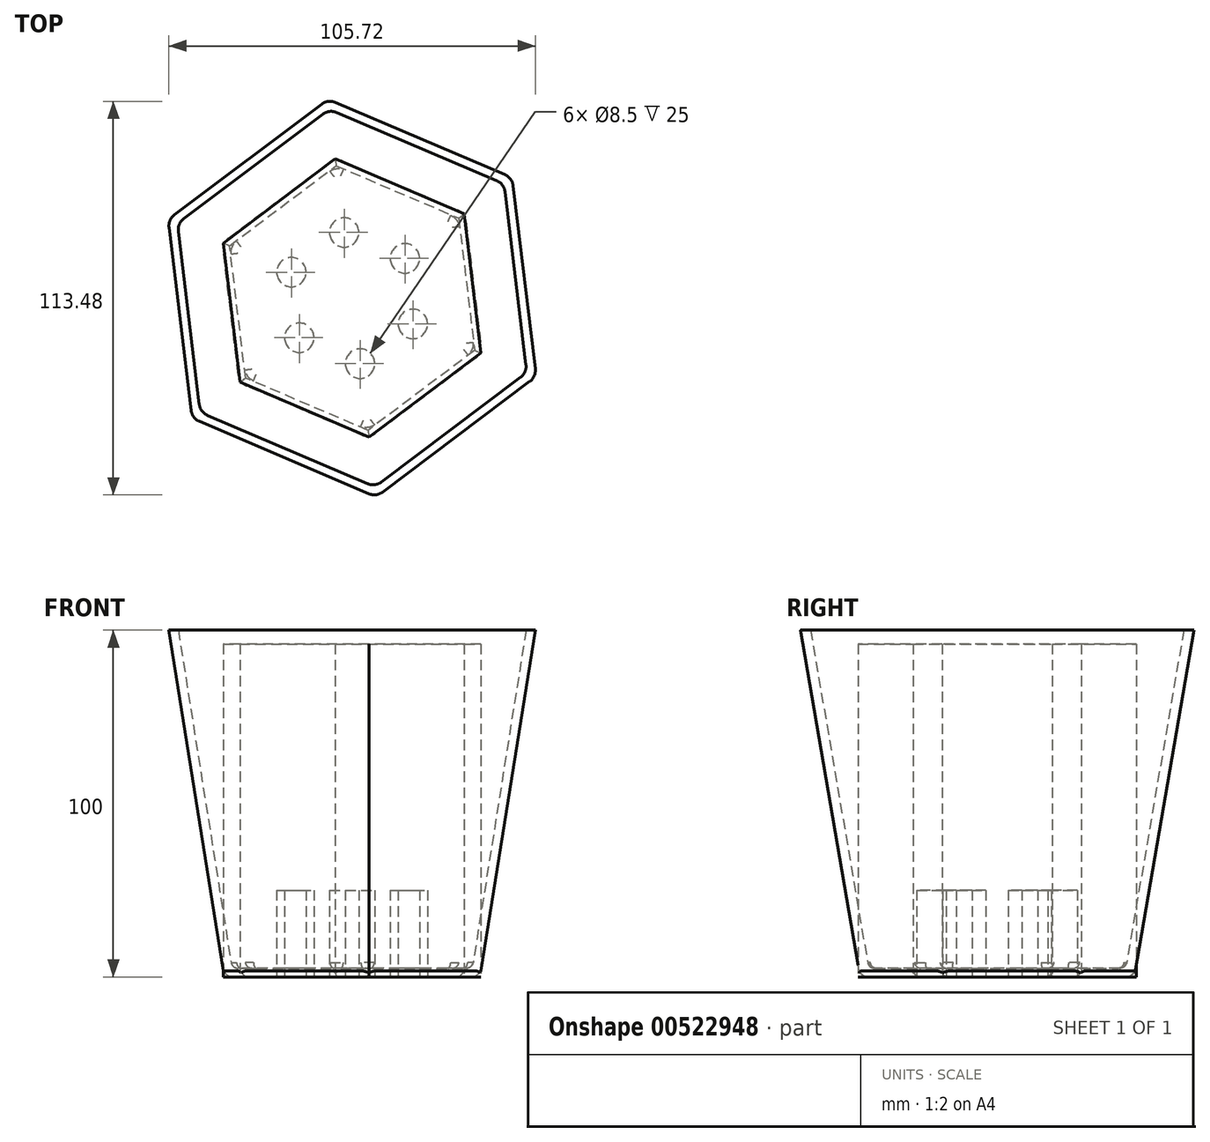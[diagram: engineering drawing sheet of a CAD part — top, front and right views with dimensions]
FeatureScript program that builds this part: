
annotation { "Feature Type Name" : "Feature", "Feature Type Description" : "" }
export const myFeature = defineFeature(function(context is Context, id is Id, definition is map)
    precondition{}
    {
        {
            var Q0;
            Q0=qCreatedBy(makeId("Top.planeOp"),FACE);
            var sketch = newSketch(context, id + "F0", { "sketchPlane" : qUnion([Q0])});
            skPoint(sketch, "E0.0.midPoint", {"position": v(32.4, 17.52) * mm});
            skCircle(sketch, "E1.cCircle", {"center": v(0, 0) * mm, "radius": 35 * mm, "construction": true});
            skLineSegment(sketch, "E1.0", {"start": v(-4.86, 40.12) * mm, "end": v(32.32, 24.27) * mm});
            skLineSegment(sketch, "E1.1", {"start": v(32.32, 24.27) * mm, "end": v(37.18, -15.85) * mm});
            skLineSegment(sketch, "E1.2", {"start": v(37.18, -15.85) * mm, "end": v(4.86, -40.12) * mm});
            skLineSegment(sketch, "E1.3", {"start": v(4.86, -40.12) * mm, "end": v(-32.32, -24.27) * mm});
            skLineSegment(sketch, "E1.4", {"start": v(-32.32, -24.27) * mm, "end": v(-37.18, 15.85) * mm});
            skLineSegment(sketch, "E1.5", {"start": v(-37.18, 15.85) * mm, "end": v(-4.86, 40.12) * mm});
            skPoint(sketch, "E1.0.midPoint", {"position": v(13.73, 32.2) * mm});
            skSolve(sketch);
        }
        {
            var Q0;
            Q0=makeQuery(id+"F0.imprint","IMPRINT",FACE,{"disambiguationData":[TD([[makeQuery(id+"F0.imprint","IMPRINT",EDGE,{"derivedFrom":sQuery(id+"F0.wireOp",EDGE,"E0.0")}),-1.0]])]});
            var Q1;
            Q1=makeQuery(id+"F0.imprint","IMPRINT",FACE,{"disambiguationData":[TD([[makeQuery(id+"F0.imprint","IMPRINT",EDGE,{"derivedFrom":sQuery(id+"F0.wireOp",EDGE,"E1.0")}),-1.0]])]});
            extrude(context, id + "F1", {"entities" : qUnion([Q0, Q1]), "depth" : 96 * mm, "offsetDistance" : 25 * mm});
        }
        {
            var Q0;
            Q0=makeQuery(id+"F1.opExtrude","CAP_FACE",FACE,{"disambiguationData":[OSD([sQuery(id+"F0.wireOp",EDGE,"E1.0"),sQuery(id+"F0.wireOp",EDGE,"E1.1"),sQuery(id+"F0.wireOp",EDGE,"E1.2"),sQuery(id+"F0.wireOp",EDGE,"E1.3"),sQuery(id+"F0.wireOp",EDGE,"E1.4"),sQuery(id+"F0.wireOp",EDGE,"E1.5")])],"isStart":false});
            var sketch = newSketch(context, id + "F2", { "sketchPlane" : qUnion([Q0])});
            skCircle(sketch, "E2.cCircle", {"center": v(0, 0) * mm, "radius": 50 * mm, "construction": true});
            skLineSegment(sketch, "E2.0", {"start": v(-6.94, 57.32) * mm, "end": v(46.17, 34.67) * mm});
            skLineSegment(sketch, "E2.1", {"start": v(46.17, 34.67) * mm, "end": v(53.1, -22.65) * mm});
            skLineSegment(sketch, "E2.2", {"start": v(53.1, -22.65) * mm, "end": v(6.94, -57.32) * mm});
            skLineSegment(sketch, "E2.3", {"start": v(6.94, -57.32) * mm, "end": v(-46.17, -34.67) * mm});
            skLineSegment(sketch, "E2.4", {"start": v(-46.17, -34.67) * mm, "end": v(-53.1, 22.65) * mm});
            skLineSegment(sketch, "E2.5", {"start": v(-53.1, 22.65) * mm, "end": v(-6.94, 57.32) * mm});
            skPoint(sketch, "E2.0.midPoint", {"position": v(19.61, 46) * mm});
            skSolve(sketch);
        }
        {
            var Q0;
            Q0 = qSketchRegion(id + "F2", true);
            extrude(context, id + "F3", {"entities" : qUnion([Q0]), "depth" : 4 * mm, "offsetDistance" : 25 * mm});
        }
        {
            var Q0;
            Q0=makeQuery(id+"F1.opExtrude","CAP_FACE",FACE,{"disambiguationData":[OSD([sQuery(id+"F0.wireOp",EDGE,"E1.0"),sQuery(id+"F0.wireOp",EDGE,"E1.1"),sQuery(id+"F0.wireOp",EDGE,"E1.2"),sQuery(id+"F0.wireOp",EDGE,"E1.3"),sQuery(id+"F0.wireOp",EDGE,"E1.4"),sQuery(id+"F0.wireOp",EDGE,"E1.5")])],"isStart":true});
            var Q1;
            Q1=makeQuery(id+"F3.opExtrude","CAP_FACE",FACE,{"disambiguationData":[OSD([sQuery(id+"F2.wireOp",EDGE,"E2.0"),sQuery(id+"F2.wireOp",EDGE,"E2.1"),sQuery(id+"F2.wireOp",EDGE,"E2.2"),sQuery(id+"F2.wireOp",EDGE,"E2.3"),sQuery(id+"F2.wireOp",EDGE,"E2.4"),sQuery(id+"F2.wireOp",EDGE,"E2.5")])],"isStart":false});
            loft(context, id + "F4", {"sheetProfilesArray" : [{ "sheetProfileEntities" : qUnion([Q0]) }, { "sheetProfileEntities" : qUnion([Q1]) }]});
        }
        {
            var Q0;
            Q0=makeQuery(id+"F3.opExtrude","SWEPT_BODY",BODY,{"disambiguationData":[OSD([sQuery(id+"F2.wireOp",EDGE,"E2.0"),sQuery(id+"F2.wireOp",EDGE,"E2.1"),sQuery(id+"F2.wireOp",EDGE,"E2.2"),sQuery(id+"F2.wireOp",EDGE,"E2.3"),sQuery(id+"F2.wireOp",EDGE,"E2.4"),sQuery(id+"F2.wireOp",EDGE,"E2.5")])]});
            deleteBodies(context, id + "F5", {"entities" : qUnion([Q0])});
        }
        {
            var Q0;
            Q0=makeQuery(id+"F4.opLoft","CAP_FACE",FACE,{"disambiguationData":[OSD([sQuery(id+"F2.wireOp",EDGE,"E2.0"),sQuery(id+"F2.wireOp",EDGE,"E2.1"),sQuery(id+"F2.wireOp",EDGE,"E2.2"),sQuery(id+"F2.wireOp",EDGE,"E2.3"),sQuery(id+"F2.wireOp",EDGE,"E2.4"),sQuery(id+"F2.wireOp",EDGE,"E2.5")])],"isStart":true});
            shell(context, id + "F6", {"entities" : qUnion([Q0]), "thickness" : 2.5 * mm});
        }
        {
            var Q0;
            Q0=makeQuery(id+"F4.opLoft","MID_CAP_EDGE",EDGE,{"disambiguationData":[OSD([sQuery(id+"F0.wireOp",EDGE,"E1.3"),sQuery(id+"F0.wireOp",EDGE,"E1.4"),sQuery(id+"F0.wireOp",EDGE,"E1.5")])],"capPos":0.0});
            var Q1;
            Q1=makeQuery(id+"F4.opLoft","MID_CAP_EDGE",EDGE,{"disambiguationData":[OSD([sQuery(id+"F0.wireOp",EDGE,"E1.2"),sQuery(id+"F0.wireOp",EDGE,"E1.3"),sQuery(id+"F0.wireOp",EDGE,"E1.4")])],"capPos":0.0});
            var Q2;
            Q2=makeQuery(id+"F4.opLoft","MID_CAP_EDGE",EDGE,{"disambiguationData":[OSD([sQuery(id+"F0.wireOp",EDGE,"E1.1"),sQuery(id+"F0.wireOp",EDGE,"E1.2"),sQuery(id+"F0.wireOp",EDGE,"E1.3")])],"capPos":0.0});
            var Q3;
            Q3=makeQuery(id+"F4.opLoft","MID_CAP_EDGE",EDGE,{"disambiguationData":[OSD([sQuery(id+"F0.wireOp",EDGE,"E1.0"),sQuery(id+"F0.wireOp",EDGE,"E1.1"),sQuery(id+"F0.wireOp",EDGE,"E1.2")])],"capPos":0.0});
            var Q4;
            Q4=makeQuery(id+"F4.opLoft","MID_CAP_EDGE",EDGE,{"disambiguationData":[OSD([sQuery(id+"F0.wireOp",EDGE,"E1.0"),sQuery(id+"F0.wireOp",EDGE,"E1.1"),sQuery(id+"F0.wireOp",EDGE,"E1.5")])],"capPos":0.0});
            var Q5;
            Q5=makeQuery(id+"F4.opLoft","MID_CAP_EDGE",EDGE,{"disambiguationData":[OSD([sQuery(id+"F0.wireOp",EDGE,"E1.0"),sQuery(id+"F0.wireOp",EDGE,"E1.4"),sQuery(id+"F0.wireOp",EDGE,"E1.5")])],"capPos":0.0});
            chamfer(context, id + "F7", {"entities" : qUnion([Q0, Q1, Q2, Q3, Q4, Q5]), "width" : 2 * mm, "tangentPropagation" : true});
        }
        {
            var Q0;
            Q0=makeQuery(id+"F4.opLoft","SWEPT_EDGE",EDGE,{"disambiguationData":[OSD([sQuery(id+"F0.wireOp",EDGE,"E1.4"),sQuery(id+"F0.wireOp",EDGE,"E1.5"),sQuery(id+"F2.wireOp",EDGE,"E2.4"),sQuery(id+"F2.wireOp",EDGE,"E2.5")])]});
            var Q1;
            Q1=makeQuery(id+"F4.opLoft","SWEPT_EDGE",EDGE,{"disambiguationData":[OSD([sQuery(id+"F0.wireOp",EDGE,"E1.3"),sQuery(id+"F0.wireOp",EDGE,"E1.4"),sQuery(id+"F2.wireOp",EDGE,"E2.3"),sQuery(id+"F2.wireOp",EDGE,"E2.4")])]});
            var Q2;
            Q2=makeQuery(id+"F4.opLoft","SWEPT_EDGE",EDGE,{"disambiguationData":[OSD([sQuery(id+"F0.wireOp",EDGE,"E1.2"),sQuery(id+"F0.wireOp",EDGE,"E1.3"),sQuery(id+"F2.wireOp",EDGE,"E2.2"),sQuery(id+"F2.wireOp",EDGE,"E2.3")])]});
            var Q3;
            Q3=makeQuery(id+"F4.opLoft","SWEPT_EDGE",EDGE,{"disambiguationData":[OSD([sQuery(id+"F0.wireOp",EDGE,"E1.1"),sQuery(id+"F0.wireOp",EDGE,"E1.2"),sQuery(id+"F2.wireOp",EDGE,"E2.1"),sQuery(id+"F2.wireOp",EDGE,"E2.2")])]});
            var Q4;
            Q4=makeQuery(id+"F4.opLoft","SWEPT_EDGE",EDGE,{"disambiguationData":[OSD([sQuery(id+"F0.wireOp",EDGE,"E1.0"),sQuery(id+"F0.wireOp",EDGE,"E1.1"),sQuery(id+"F2.wireOp",EDGE,"E2.0"),sQuery(id+"F2.wireOp",EDGE,"E2.1")])]});
            var Q5;
            Q5=makeQuery(id+"F4.opLoft","SWEPT_EDGE",EDGE,{"disambiguationData":[OSD([sQuery(id+"F0.wireOp",EDGE,"E1.0"),sQuery(id+"F0.wireOp",EDGE,"E1.5"),sQuery(id+"F2.wireOp",EDGE,"E2.0"),sQuery(id+"F2.wireOp",EDGE,"E2.5")])]});
            var Q6;
            Q6=makeQuery(id+"F6.opShell","OFFSET_EDGE",EDGE,{"disambiguationData":[OSD([sQuery(id+"F0.wireOp",EDGE,"E1.0"),sQuery(id+"F0.wireOp",EDGE,"E1.5"),sQuery(id+"F2.wireOp",EDGE,"E2.0"),sQuery(id+"F2.wireOp",EDGE,"E2.5")])]});
            var Q7;
            Q7=makeQuery(id+"F6.opShell","OFFSET_EDGE",EDGE,{"disambiguationData":[OSD([sQuery(id+"F0.wireOp",EDGE,"E1.0"),sQuery(id+"F0.wireOp",EDGE,"E1.1"),sQuery(id+"F2.wireOp",EDGE,"E2.0"),sQuery(id+"F2.wireOp",EDGE,"E2.1")])]});
            var Q8;
            Q8=makeQuery(id+"F6.opShell","OFFSET_EDGE",EDGE,{"disambiguationData":[OSD([sQuery(id+"F0.wireOp",EDGE,"E1.1"),sQuery(id+"F0.wireOp",EDGE,"E1.2"),sQuery(id+"F2.wireOp",EDGE,"E2.1"),sQuery(id+"F2.wireOp",EDGE,"E2.2")])]});
            var Q9;
            Q9=makeQuery(id+"F6.opShell","OFFSET_EDGE",EDGE,{"disambiguationData":[OSD([sQuery(id+"F0.wireOp",EDGE,"E1.2"),sQuery(id+"F0.wireOp",EDGE,"E1.3"),sQuery(id+"F2.wireOp",EDGE,"E2.2"),sQuery(id+"F2.wireOp",EDGE,"E2.3")])]});
            var Q10;
            Q10=makeQuery(id+"F6.opShell","OFFSET_EDGE",EDGE,{"disambiguationData":[OSD([sQuery(id+"F0.wireOp",EDGE,"E1.3"),sQuery(id+"F0.wireOp",EDGE,"E1.4"),sQuery(id+"F2.wireOp",EDGE,"E2.3"),sQuery(id+"F2.wireOp",EDGE,"E2.4")])]});
            var Q11;
            Q11=makeQuery(id+"F6.opShell","OFFSET_EDGE",EDGE,{"disambiguationData":[OSD([sQuery(id+"F0.wireOp",EDGE,"E1.4"),sQuery(id+"F0.wireOp",EDGE,"E1.5"),sQuery(id+"F2.wireOp",EDGE,"E2.4"),sQuery(id+"F2.wireOp",EDGE,"E2.5")])]});
            fillet(context, id + "F8", {"entities" : qUnion([Q0, Q1, Q2, Q3, Q4, Q5, Q6, Q7, Q8, Q9, Q10, Q11]), "radius" : 4 * mm, "tangentPropagation" : true, "allowEdgeOverflow" : false});
        }
        {
            var Q0;
            Q0=makeQuery(id+"F6.opShell","OFFSET_EDGE",EDGE,{"disambiguationData":[OSD([sQuery(id+"F0.wireOp",EDGE,"E1.0"),sQuery(id+"F0.wireOp",EDGE,"E1.4"),sQuery(id+"F0.wireOp",EDGE,"E1.5")])]});
            var Q1;
            {var subQ0=sQuery(id+"F0.wireOp",EDGE,"E1.5");var subQ1=sQuery(id+"F0.wireOp",EDGE,"E1.0");Q1=makeQuery(id+"F8.opFillet","BLEND_EDGE",EDGE,{"blendedFrom":[makeQuery(id+"F6.opShell","OFFSET_EDGE",EDGE,{"disambiguationData":[OSD([subQ1,subQ0,sQuery(id+"F2.wireOp",EDGE,"E2.0"),sQuery(id+"F2.wireOp",EDGE,"E2.5")])]}),makeQuery(id+"F6.opShell","OFFSET_FACE",FACE,{"disambiguationData":[OSD([subQ1,sQuery(id+"F0.wireOp",EDGE,"E1.1"),sQuery(id+"F0.wireOp",EDGE,"E1.2"),sQuery(id+"F0.wireOp",EDGE,"E1.3"),sQuery(id+"F0.wireOp",EDGE,"E1.4"),subQ0])]})],"blendedInto":[makeQuery(id+"F6.opShell","OFFSET_FACE",FACE,{"disambiguationData":[OSD([subQ1,sQuery(id+"F0.wireOp",EDGE,"E1.1"),sQuery(id+"F0.wireOp",EDGE,"E1.2"),sQuery(id+"F0.wireOp",EDGE,"E1.3"),sQuery(id+"F0.wireOp",EDGE,"E1.4"),subQ0])]})]});}
            var Q2;
            Q2=makeQuery(id+"F6.opShell","OFFSET_EDGE",EDGE,{"disambiguationData":[OSD([sQuery(id+"F0.wireOp",EDGE,"E1.0"),sQuery(id+"F0.wireOp",EDGE,"E1.1"),sQuery(id+"F0.wireOp",EDGE,"E1.5")])]});
            var Q3;
            {var subQ0=sQuery(id+"F0.wireOp",EDGE,"E1.1");var subQ1=sQuery(id+"F0.wireOp",EDGE,"E1.0");Q3=makeQuery(id+"F8.opFillet","BLEND_EDGE",EDGE,{"blendedFrom":[makeQuery(id+"F6.opShell","OFFSET_EDGE",EDGE,{"disambiguationData":[OSD([subQ1,subQ0,sQuery(id+"F2.wireOp",EDGE,"E2.0"),sQuery(id+"F2.wireOp",EDGE,"E2.1")])]}),makeQuery(id+"F6.opShell","OFFSET_FACE",FACE,{"disambiguationData":[OSD([subQ1,subQ0,sQuery(id+"F0.wireOp",EDGE,"E1.2"),sQuery(id+"F0.wireOp",EDGE,"E1.3"),sQuery(id+"F0.wireOp",EDGE,"E1.4"),sQuery(id+"F0.wireOp",EDGE,"E1.5")])]})],"blendedInto":[makeQuery(id+"F6.opShell","OFFSET_FACE",FACE,{"disambiguationData":[OSD([subQ1,subQ0,sQuery(id+"F0.wireOp",EDGE,"E1.2"),sQuery(id+"F0.wireOp",EDGE,"E1.3"),sQuery(id+"F0.wireOp",EDGE,"E1.4"),sQuery(id+"F0.wireOp",EDGE,"E1.5")])]})]});}
            var Q4;
            Q4=makeQuery(id+"F6.opShell","OFFSET_EDGE",EDGE,{"disambiguationData":[OSD([sQuery(id+"F0.wireOp",EDGE,"E1.0"),sQuery(id+"F0.wireOp",EDGE,"E1.1"),sQuery(id+"F0.wireOp",EDGE,"E1.2")])]});
            var Q5;
            {var subQ0=sQuery(id+"F0.wireOp",EDGE,"E1.2");var subQ1=sQuery(id+"F0.wireOp",EDGE,"E1.1");Q5=makeQuery(id+"F8.opFillet","BLEND_EDGE",EDGE,{"blendedFrom":[makeQuery(id+"F6.opShell","OFFSET_EDGE",EDGE,{"disambiguationData":[OSD([subQ1,subQ0,sQuery(id+"F2.wireOp",EDGE,"E2.1"),sQuery(id+"F2.wireOp",EDGE,"E2.2")])]}),makeQuery(id+"F6.opShell","OFFSET_FACE",FACE,{"disambiguationData":[OSD([sQuery(id+"F0.wireOp",EDGE,"E1.0"),subQ1,subQ0,sQuery(id+"F0.wireOp",EDGE,"E1.3"),sQuery(id+"F0.wireOp",EDGE,"E1.4"),sQuery(id+"F0.wireOp",EDGE,"E1.5")])]})],"blendedInto":[makeQuery(id+"F6.opShell","OFFSET_FACE",FACE,{"disambiguationData":[OSD([sQuery(id+"F0.wireOp",EDGE,"E1.0"),subQ1,subQ0,sQuery(id+"F0.wireOp",EDGE,"E1.3"),sQuery(id+"F0.wireOp",EDGE,"E1.4"),sQuery(id+"F0.wireOp",EDGE,"E1.5")])]})]});}
            var Q6;
            Q6=makeQuery(id+"F6.opShell","OFFSET_EDGE",EDGE,{"disambiguationData":[OSD([sQuery(id+"F0.wireOp",EDGE,"E1.1"),sQuery(id+"F0.wireOp",EDGE,"E1.2"),sQuery(id+"F0.wireOp",EDGE,"E1.3")])]});
            var Q7;
            Q7=makeQuery(id+"F6.opShell","OFFSET_EDGE",EDGE,{"disambiguationData":[OSD([sQuery(id+"F0.wireOp",EDGE,"E1.2"),sQuery(id+"F0.wireOp",EDGE,"E1.3"),sQuery(id+"F0.wireOp",EDGE,"E1.4")])]});
            var Q8;
            Q8=makeQuery(id+"F6.opShell","OFFSET_EDGE",EDGE,{"disambiguationData":[OSD([sQuery(id+"F0.wireOp",EDGE,"E1.3"),sQuery(id+"F0.wireOp",EDGE,"E1.4"),sQuery(id+"F0.wireOp",EDGE,"E1.5")])]});
            var Q9;
            {var subQ0=sQuery(id+"F0.wireOp",EDGE,"E1.5");var subQ1=sQuery(id+"F0.wireOp",EDGE,"E1.4");Q9=makeQuery(id+"F8.opFillet","BLEND_EDGE",EDGE,{"blendedFrom":[makeQuery(id+"F6.opShell","OFFSET_EDGE",EDGE,{"disambiguationData":[OSD([subQ1,subQ0,sQuery(id+"F2.wireOp",EDGE,"E2.4"),sQuery(id+"F2.wireOp",EDGE,"E2.5")])]}),makeQuery(id+"F6.opShell","OFFSET_FACE",FACE,{"disambiguationData":[OSD([sQuery(id+"F0.wireOp",EDGE,"E1.0"),sQuery(id+"F0.wireOp",EDGE,"E1.1"),sQuery(id+"F0.wireOp",EDGE,"E1.2"),sQuery(id+"F0.wireOp",EDGE,"E1.3"),subQ1,subQ0])]})],"blendedInto":[makeQuery(id+"F6.opShell","OFFSET_FACE",FACE,{"disambiguationData":[OSD([sQuery(id+"F0.wireOp",EDGE,"E1.0"),sQuery(id+"F0.wireOp",EDGE,"E1.1"),sQuery(id+"F0.wireOp",EDGE,"E1.2"),sQuery(id+"F0.wireOp",EDGE,"E1.3"),subQ1,subQ0])]})]});}
            var Q10;
            {var subQ0=sQuery(id+"F0.wireOp",EDGE,"E1.4");var subQ1=sQuery(id+"F0.wireOp",EDGE,"E1.3");Q10=makeQuery(id+"F8.opFillet","BLEND_EDGE",EDGE,{"blendedFrom":[makeQuery(id+"F6.opShell","OFFSET_EDGE",EDGE,{"disambiguationData":[OSD([subQ1,subQ0,sQuery(id+"F2.wireOp",EDGE,"E2.3"),sQuery(id+"F2.wireOp",EDGE,"E2.4")])]}),makeQuery(id+"F6.opShell","OFFSET_FACE",FACE,{"disambiguationData":[OSD([sQuery(id+"F0.wireOp",EDGE,"E1.0"),sQuery(id+"F0.wireOp",EDGE,"E1.1"),sQuery(id+"F0.wireOp",EDGE,"E1.2"),subQ1,subQ0,sQuery(id+"F0.wireOp",EDGE,"E1.5")])]})],"blendedInto":[makeQuery(id+"F6.opShell","OFFSET_FACE",FACE,{"disambiguationData":[OSD([sQuery(id+"F0.wireOp",EDGE,"E1.0"),sQuery(id+"F0.wireOp",EDGE,"E1.1"),sQuery(id+"F0.wireOp",EDGE,"E1.2"),subQ1,subQ0,sQuery(id+"F0.wireOp",EDGE,"E1.5")])]})]});}
            var Q11;
            {var subQ0=sQuery(id+"F0.wireOp",EDGE,"E1.3");var subQ1=sQuery(id+"F0.wireOp",EDGE,"E1.2");Q11=makeQuery(id+"F8.opFillet","BLEND_EDGE",EDGE,{"blendedFrom":[makeQuery(id+"F6.opShell","OFFSET_EDGE",EDGE,{"disambiguationData":[OSD([subQ1,subQ0,sQuery(id+"F2.wireOp",EDGE,"E2.2"),sQuery(id+"F2.wireOp",EDGE,"E2.3")])]}),makeQuery(id+"F6.opShell","OFFSET_FACE",FACE,{"disambiguationData":[OSD([sQuery(id+"F0.wireOp",EDGE,"E1.0"),sQuery(id+"F0.wireOp",EDGE,"E1.1"),subQ1,subQ0,sQuery(id+"F0.wireOp",EDGE,"E1.4"),sQuery(id+"F0.wireOp",EDGE,"E1.5")])]})],"blendedInto":[makeQuery(id+"F6.opShell","OFFSET_FACE",FACE,{"disambiguationData":[OSD([sQuery(id+"F0.wireOp",EDGE,"E1.0"),sQuery(id+"F0.wireOp",EDGE,"E1.1"),subQ1,subQ0,sQuery(id+"F0.wireOp",EDGE,"E1.4"),sQuery(id+"F0.wireOp",EDGE,"E1.5")])]})]});}
            fillet(context, id + "F9", {"entities" : qUnion([Q0, Q1, Q2, Q3, Q4, Q5, Q6, Q7, Q8, Q9, Q10, Q11]), "radius" : 2 * mm, "tangentPropagation" : true, "allowEdgeOverflow" : false});
        }
        {
            var Q0;
            Q0=makeQuery(id+"F4.opLoft","CAP_FACE",FACE,{"disambiguationData":[OSD([sQuery(id+"F0.wireOp",EDGE,"E1.0"),sQuery(id+"F0.wireOp",EDGE,"E1.1"),sQuery(id+"F0.wireOp",EDGE,"E1.2"),sQuery(id+"F0.wireOp",EDGE,"E1.3"),sQuery(id+"F0.wireOp",EDGE,"E1.4"),sQuery(id+"F0.wireOp",EDGE,"E1.5")])],"isStart":true});
            var sketch = newSketch(context, id + "F10", { "sketchPlane" : qUnion([Q0])});
            skCircle(sketch, "E3", {"center": v(-2.3, -18.91) * mm, "radius": 4.25 * mm});
            skCircle(sketch, "E4", {"center": v(-17.53, -7.47) * mm, "radius": 4.25 * mm});
            skCircle(sketch, "E5", {"center": v(-15.23, 11.44) * mm, "radius": 4.25 * mm});
            skCircle(sketch, "E6", {"center": v(2.3, 18.91) * mm, "radius": 4.25 * mm});
            skCircle(sketch, "E7", {"center": v(17.53, 7.47) * mm, "radius": 4.25 * mm});
            skCircle(sketch, "E8", {"center": v(15.23, -11.44) * mm, "radius": 4.25 * mm});
            skSolve(sketch);
        }
        {
            var Q0;
            Q0 = qSketchRegion(id + "F10", true);
            extrude(context, id + "F11", {"entities" : qUnion([Q0]), "operationType" : NewBodyOperationType.REMOVE, "oppositeDirection" : true, "depth" : 25 * mm, "offsetDistance" : 25 * mm});
        }
    });
